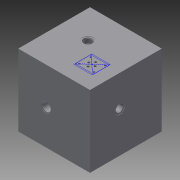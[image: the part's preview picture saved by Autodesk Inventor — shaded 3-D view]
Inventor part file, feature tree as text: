
AUTODESK INVENTOR PART (.ipt)
format: ipt  version: 2014 (Build 180170000, 170)  size: 437,760 bytes
history: native  units: mm
features: other x50, sketch x6, extrude x1
ambient origin geometry x8: Origin, YZ Plane, XZ Plane, XY Plane, X Axis, Y Axis, Z Axis, Center Point
bodies: 实体1 (feature_tree)
feature tree (57):
  extrude  "拉伸1"  TaperAngle=0.0deg  [1 undecoded]
  other  "UCS1"
  other  "UCS2"
  other  "UCS3"
  other  "UCS4"
  other  "UCS5"
  other  "UCS6"
  other  "Footprint6"
  other  "Footprint5"
  sketch  "草图1"  dims[d0=200.0mm d1=0.0mm]
  other  "UCS1: YZ 平面"
  other  "UCS1: XZ 平面"
  other  "UCS1: XY 平面"
  other  "UCS1: X 轴"
  other  "UCS1: Y 轴"
  other  "UCS1: Z 轴"
  other  "UCS1: 原点"
  other  "UCS2: YZ 平面"
  other  "UCS2: XZ 平面"
  other  "UCS2: XY 平面"
  other  "UCS2: X 轴"
  other  "UCS2: Y 轴"
  other  "UCS2: Z 轴"
  other  "UCS2: 原点"
  other  "UCS3: YZ 平面"
  other  "UCS3: XZ 平面"
  other  "UCS3: XY 平面"
  other  "UCS3: X 轴"
  other  "UCS3: Y 轴"
  other  "UCS3: Z 轴"
  other  "UCS3: 原点"
  other  "UCS4: YZ 平面"
  other  "UCS4: XZ 平面"
  other  "UCS4: XY 平面"
  other  "UCS4: X 轴"
  other  "UCS4: Y 轴"
  other  "UCS4: Z 轴"
  other  "UCS4: 原点"
  other  "UCS5: YZ 平面"
  other  "UCS5: XZ 平面"
  other  "UCS5: XY 平面"
  other  "UCS5: X 轴"
  other  "UCS5: Y 轴"
  other  "UCS5: Z 轴"
  other  "UCS5: 原点"
  other  "UCS6: YZ 平面"
  other  "UCS6: XZ 平面"
  other  "UCS6: XY 平面"
  other  "UCS6: X 轴"
  other  "UCS6: Y 轴"
  other  "UCS6: Z 轴"
  other  "UCS6: 原点"
  sketch  "草图2"  dims[d2=0.0mm d3=0.0mm d4=0.0mm d5=0.0mm d6=0.0mm d7=0.0mm]
  sketch  "草图3"  dims[d8=0.0mm d9=0.0mm d10=0.0mm d11=0.0mm d12=0.0mm d13=0.0mm]
  sketch  "草图4"  dims[d14=0.0mm d15=0.0mm d16=0.0mm d17=0.0mm d18=0.0mm d19=0.0mm]
  sketch  "草图13"  dims[d20=0.0mm d21=0.0mm d22=0.0mm d23=0.0mm d24=0.0mm d25=0.0mm]
  sketch  "草图17"  dims[d26=0.0mm d27=0.0mm d28=0.0mm d29=0.0mm d30=0.0mm d31=0.0mm d32=0.0mm d33=0.0mm d34=0.0mm d35=0.0mm d36=0.0mm d37=0.0mm d38=0.0mm d42=0.0mm d46=0.0mm d47=0.0mm d51=0.0mm d65=0.0mm d79=0.0mm d93=0.0mm d107=0.0mm d121=0.0mm d135=0.0mm]
note: 1 required parameter value undecoded (feature->parameter linkage not recoverable at this tier; creation-order binding heuristic only, values carry confidence <= 0.55)
